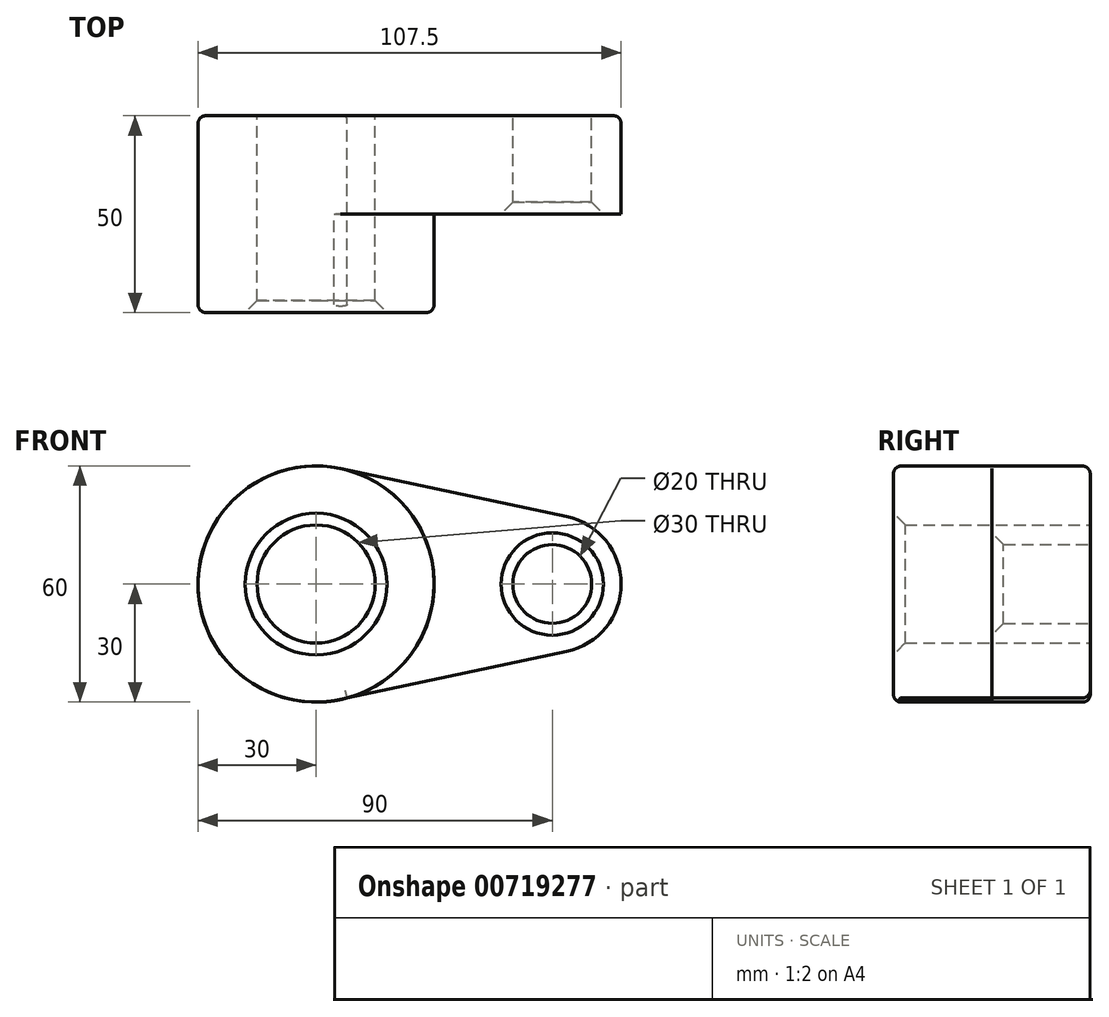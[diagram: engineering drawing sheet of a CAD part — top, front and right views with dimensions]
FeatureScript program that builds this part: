
annotation { "Feature Type Name" : "Feature", "Feature Type Description" : "" }
export const myFeature = defineFeature(function(context is Context, id is Id, definition is map)
    precondition{}
    {
        {
            var Q0;
            Q0=qCreatedBy(makeId("Front.planeOp"),FACE);
            var sketch = newSketch(context, id + "F0", { "sketchPlane" : qUnion([Q0])});
            skCircle(sketch, "E0", {"center": v(0, 0) * mm, "radius": 30 * mm});
            skCircle(sketch, "E1", {"center": v(60, 0) * mm, "radius": 17.5 * mm});
            skLineSegment(sketch, "E2", {"start": v(6.25, 29.34) * mm, "end": v(63.65, 17.12) * mm});
            skCircle(sketch, "E3", {"center": v(0, 0) * mm, "radius": 15 * mm});
            skCircle(sketch, "E4", {"center": v(60, 0) * mm, "radius": 10 * mm});
            skLineSegment(sketch, "E5", {"start": v(4.53, -29.66) * mm, "end": v(63.63, -17.12) * mm});
            skSolve(sketch);
        }
        {
            var Q0;
            Q0 = qSketchRegion(id + "F0", true);
            extrude(context, id + "F1", {"entities" : qUnion([Q0]), "depth" : 25 * mm, "offsetDistance" : 25.4 * mm});
        }
        {
            var Q0;
            Q0=makeQuery(id+"F0.imprint","IMPRINT",FACE,{"disambiguationData":[TD([[makeQuery(id+"F0.imprint","IMPRINT",EDGE,{"derivedFrom":sQuery(id+"F0.wireOp",EDGE,"E3")}),-1.0]])]});
            extrude(context, id + "F2", {"entities" : qUnion([Q0]), "operationType" : NewBodyOperationType.ADD, "depth" : 50 * mm, "offsetDistance" : 25.4 * mm});
        }
        {
            var Q0;
            Q0=makeQuery(id+"F1.opExtrude","CAP_EDGE",EDGE,{"disambiguationData":[OSD([sQuery(id+"F0.wireOp",EDGE,"E0")])],"isStart":true});
            var Q1;
            Q1=makeQuery(id+"F1.opExtrude","CAP_EDGE",EDGE,{"disambiguationData":[OSD([sQuery(id+"F0.wireOp",EDGE,"2QynCXxk-8jc6-VGWg-qsRq-TrCqIErvxN5i")])],"isStart":true});
            var Q2;
            Q2=makeQuery(id+"F1.opExtrude","CAP_EDGE",EDGE,{"disambiguationData":[OSD([sQuery(id+"F0.wireOp",EDGE,"E1")])],"isStart":true});
            var Q3;
            Q3=makeQuery(id+"F1.opExtrude","CAP_EDGE",EDGE,{"disambiguationData":[OSD([sQuery(id+"F0.wireOp",EDGE,"E2")])],"isStart":true});
            var Q4;
            Q4=makeQuery(id+"F2.opExtrude","CAP_EDGE",EDGE,{"disambiguationData":[OSD([sQuery(id+"F0.wireOp",EDGE,"E0")])],"isStart":false});
            fillet(context, id + "F3", {"entities" : qUnion([Q0, Q1, Q2, Q3, Q4]), "radius" : 2 * mm, "tangentPropagation" : true, "allowEdgeOverflow" : false});
        }
        {
            var Q0;
            Q0=makeQuery(id+"F2.opExtrude","CAP_EDGE",EDGE,{"disambiguationData":[OSD([sQuery(id+"F0.wireOp",EDGE,"E3")])],"isStart":false});
            var Q1;
            Q1=makeQuery(id+"F1.opExtrude","CAP_EDGE",EDGE,{"disambiguationData":[OSD([sQuery(id+"F0.wireOp",EDGE,"E4")])],"isStart":false});
            chamfer(context, id + "F4", {"entities" : qUnion([Q0, Q1]), "width" : 3 * mm, "tangentPropagation" : true});
        }
    });
